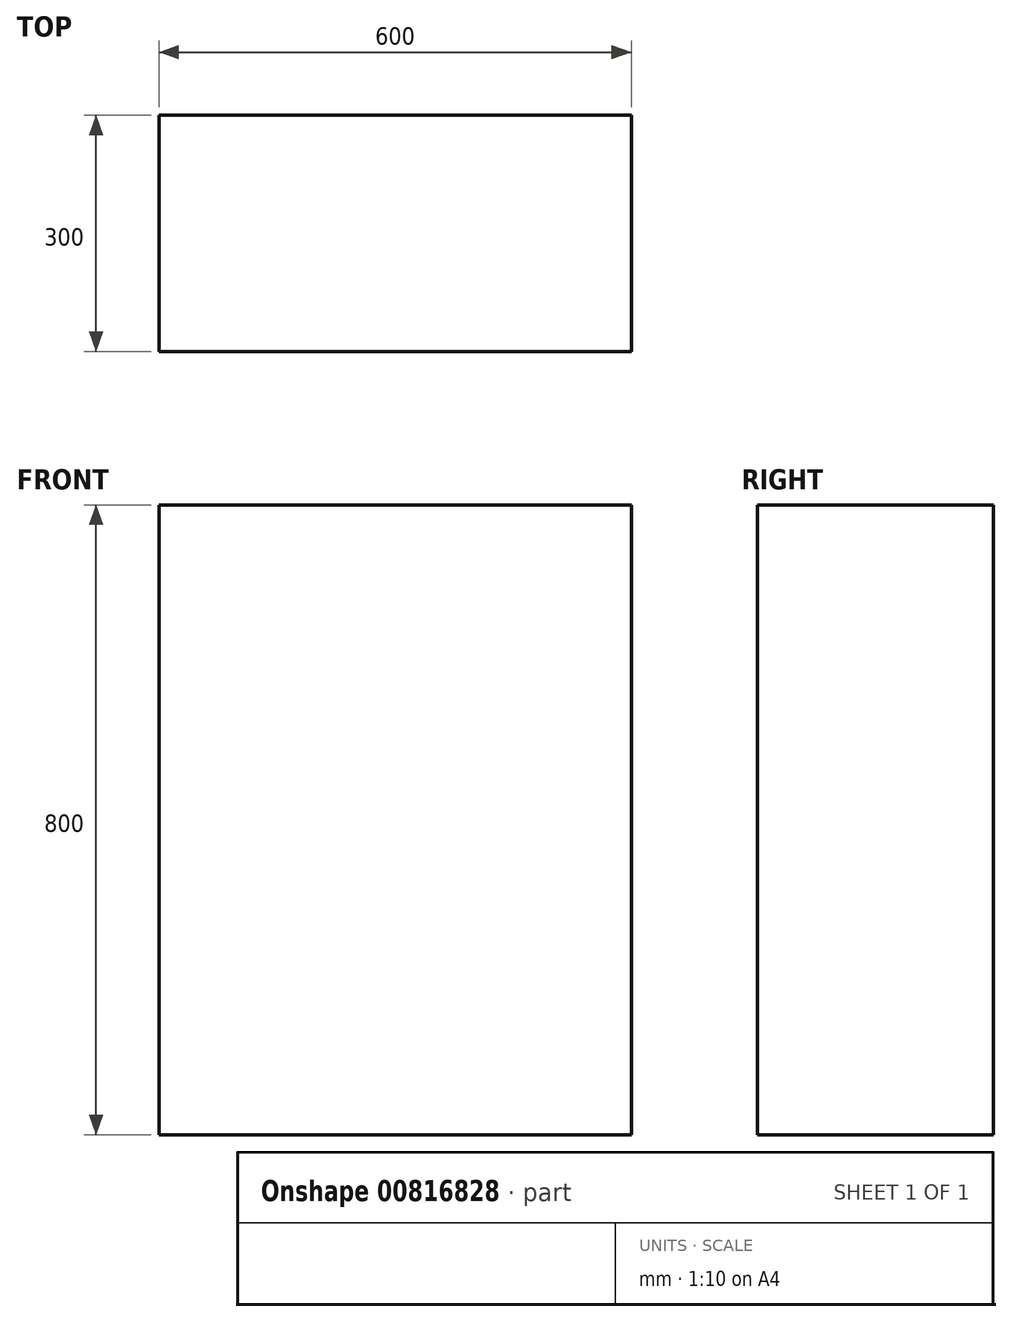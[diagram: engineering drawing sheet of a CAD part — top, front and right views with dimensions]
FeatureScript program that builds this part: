
annotation { "Feature Type Name" : "Feature", "Feature Type Description" : "" }
export const myFeature = defineFeature(function(context is Context, id is Id, definition is map)
    precondition{}
    {
        {
            var Q0;
            Q0=qCreatedBy(makeId("Front.planeOp"),FACE);
            var sketch = newSketch(context, id + "F0", { "sketchPlane" : qUnion([Q0])});
            skLineSegment(sketch, "E0.bottom", {"start": v(0, 0) * mm, "end": v(-600, 0) * mm});
            skLineSegment(sketch, "E0.top", {"start": v(0, 800) * mm, "end": v(-600, 800) * mm});
            skLineSegment(sketch, "E0.left", {"start": v(0, 0) * mm, "end": v(0, 800) * mm});
            skLineSegment(sketch, "E0.right", {"start": v(-600, 0) * mm, "end": v(-600, 800) * mm});
            skSolve(sketch);
        }
        {
            var Q0;
            Q0=makeQuery(id+"F0.imprint","IMPRINT",FACE,{"disambiguationData":[TD([[makeQuery(id+"F0.imprint","IMPRINT",EDGE,{"derivedFrom":sQuery(id+"F0.wireOp",EDGE,"E0.bottom")}),-1.0]])]});
            extrude(context, id + "F1", {"entities" : qUnion([Q0]), "depth" : 300 * mm, "offsetDistance" : 25 * mm});
        }
    });
